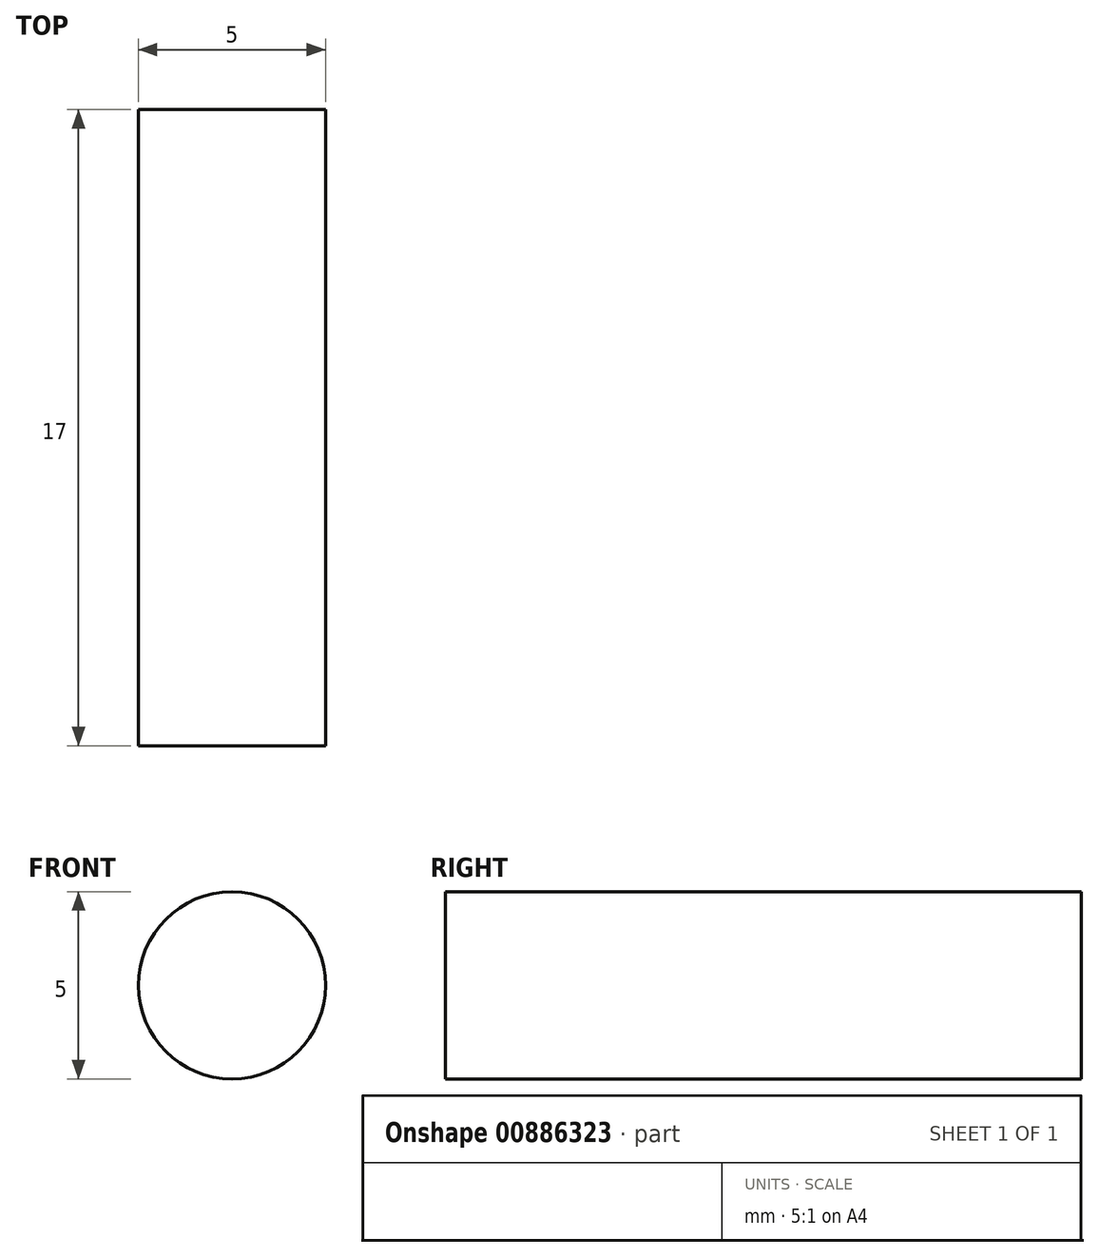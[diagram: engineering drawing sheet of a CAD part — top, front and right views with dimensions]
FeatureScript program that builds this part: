
annotation { "Feature Type Name" : "Feature", "Feature Type Description" : "" }
export const myFeature = defineFeature(function(context is Context, id is Id, definition is map)
    precondition{}
    {
        {
            var Q0;
            Q0=qCreatedBy(makeId("Front.planeOp"),FACE);
            var sketch = newSketch(context, id + "F0", { "sketchPlane" : qUnion([Q0])});
            skCircle(sketch, "E0", {"center": v(0, 0) * mm, "radius": 2.5 * mm});
            skSolve(sketch);
        }
        {
            var Q0;
            Q0 = qSketchRegion(id + "F0", true);
            extrude(context, id + "F1", {"entities" : qUnion([Q0]), "depth" : 17 * mm, "offsetDistance" : 25 * mm});
        }
    });
